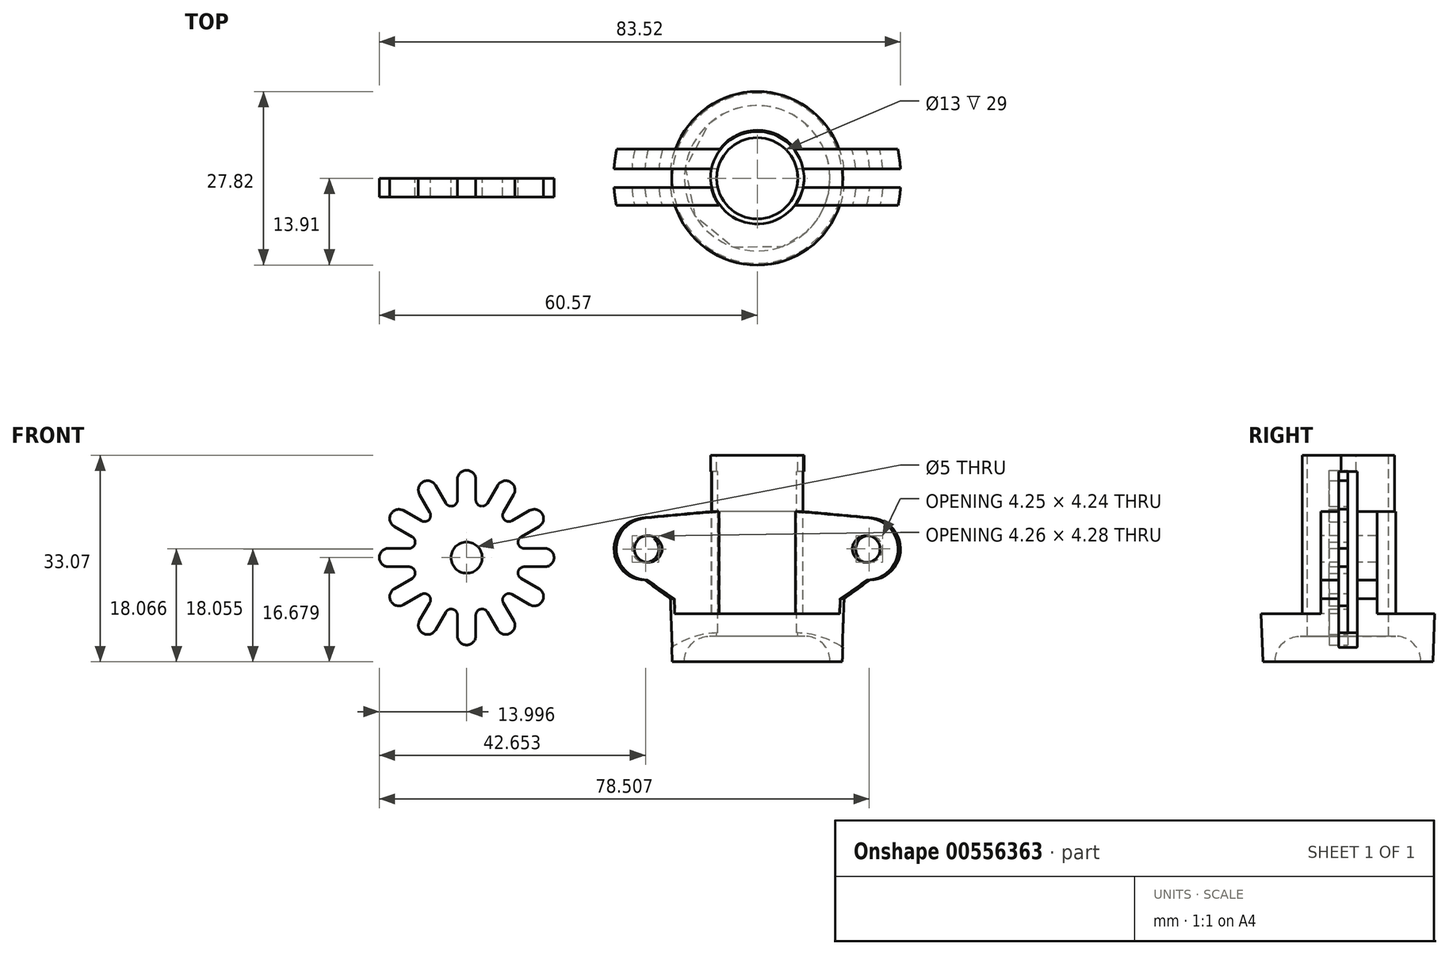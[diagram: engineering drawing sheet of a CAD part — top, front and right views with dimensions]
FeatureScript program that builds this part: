
annotation { "Feature Type Name" : "Feature", "Feature Type Description" : "" }
export const myFeature = defineFeature(function(context is Context, id is Id, definition is map)
    precondition{}
    {
        {
            var Q0;
            Q0=qCreatedBy(makeId("Front.planeOp"),FACE);
            var sketch = newSketch(context, id + "F0", { "sketchPlane" : qUnion([Q0])});
            skLineSegment(sketch, "E0", {"start": v(0, 47.2) * mm, "end": v(7.5, 47.2) * mm, "construction": true});
            skLineSegment(sketch, "E1", {"start": v(0, 38.2) * mm, "end": v(7.5, 38.2) * mm, "construction": true});
            skLineSegment(sketch, "E2", {"start": v(0, 32.2) * mm, "end": v(23, 32.2) * mm, "construction": true});
            skLineSegment(sketch, "E3", {"start": v(0, 24.2) * mm, "end": v(14, 24.2) * mm, "construction": true});
            skLineSegment(sketch, "E4", {"start": v(7.5, 47.2) * mm, "end": v(7.5, 38.2) * mm, "construction": true});
            skCircle(sketch, "E5", {"center": v(18, 32.2) * mm, "radius": 5 * mm, "construction": true});
            skLineSegment(sketch, "E6", {"start": v(7.5, 47.2) * mm, "end": v(7.5, 38.2) * mm});
            skLineSegment(sketch, "E7", {"start": v(7.5, 38.2) * mm, "end": v(18.46, 37.17) * mm});
            skArc(sketch, "E8", {"start": v(18.46, 37.17) * mm, "mid": v(23, 32) * mm, "end": v(18.07, 27.2) * mm});
            skLineSegment(sketch, "E9", {"start": v(18.07, 27.2) * mm, "end": v(14, 24.2) * mm});
            skLineSegment(sketch, "E10", {"start": v(7.5, 47.2) * mm, "end": v(6.5, 47.2) * mm});
            skLineSegment(sketch, "E11", {"start": v(6.5, 47.2) * mm, "end": v(6.5, 18.2) * mm});
            skLineSegment(sketch, "E12", {"start": v(7.66, 18.2) * mm, "end": v(6.5, 18.2) * mm});
            skPoint(sketch, "E13.visualSharp", {"position": v(11.67, 18.2) * mm});
            skArc(sketch, "E13.filletArc", {"start": v(11.66, 14.13) * mm, "mid": v(10.52, 17) * mm, "end": v(7.66, 18.2) * mm});
            skPoint(sketch, "E14", {"position": v(13.63, 14.13) * mm});
            skLineSegment(sketch, "E15", {"start": v(11.66, 14.13) * mm, "end": v(13.63, 14.13) * mm});
            skLineSegment(sketch, "E16", {"start": v(14, 24.2) * mm, "end": v(13.63, 14.13) * mm});
            skLineSegment(sketch, "E17", {"start": v(0, 61.24) * mm, "end": v(0, 0) * mm, "construction": true});
            skCircle(sketch, "E18", {"center": v(18, 32.2) * mm, "radius": 2.15 * mm});
            skSolve(sketch);
        }
        {
            var Q0;
            Q0 = qSketchRegion(id + "F0", true);
            var Q1;
            Q1=sQuery(id+"F0.wireOp",EDGE,"E17");
            revolve(context, id + "F1", {"entities" : qUnion([Q0]), "axis" : qUnion([Q1]), "revolveType" : RevolveType.FULL});
        }
        {
            var Q0;
            Q0=makeQuery(id+"F1.opRevolve","SWEPT_FACE",FACE,{"disambiguationData":[OSD([sQuery(id+"F0.wireOp",EDGE,"E10")])]});
            var sketch = newSketch(context, id + "F2", { "sketchPlane" : qUnion([Q0])});
            skCircle(sketch, "E19.0", {"center": v(0.03, 0.18) * mm, "radius": 7.5 * mm});
            skCircle(sketch, "E20", {"center": v(0.03, 0.18) * mm, "radius": 23.76 * mm});
            skLineSegment(sketch, "E21", {"start": v(25.7, 0.18) * mm, "end": v(-26.86, 0.18) * mm, "construction": true});
            skLineSegment(sketch, "E22", {"start": v(23.36, 4.68) * mm, "end": v(6.03, 4.68) * mm});
            skLineSegment(sketch, "E23.trimOffspring", {"start": v(-5.97, 4.68) * mm, "end": v(-23.3, 4.68) * mm});
            skLineSegment(sketch, "E24.MirrorCS", {"start": v(-5.97, -4.32) * mm, "end": v(-23.3, -4.32) * mm});
            skLineSegment(sketch, "E25.MirrorCS", {"start": v(23.36, -4.32) * mm, "end": v(6.03, -4.32) * mm});
            skSolve(sketch);
        }
        {
            var Q0;
            {var subQ0=sQuery(id+"F2.wireOp",EDGE,"E22");Q0=makeQuery(id+"F2.imprint","IMPRINT",FACE,{"disambiguationData":[TD([[makeQuery(id+"F2.imprint","IMPRINT",EDGE,{"derivedFrom":subQ0}),-1.0]])]});}
            var Q1;
            {var subQ0=sQuery(id+"F2.wireOp",EDGE,"E24.MirrorCS");var subQ1=sQuery(id+"F2.wireOp",EDGE,"E19.0");var subQ2=makeQuery(id+"F2.imprint","INTERSECT",VERTEX,{"derivedFrom":[subQ1,subQ0]});Q1=makeQuery(id+"F2.imprint","IMPRINT",FACE,{"disambiguationData":[TD([[makeQuery(id+"F2.imprint","IMPRINT",EDGE,{"disambiguationData":[TD([[subQ2,1.0]])],"derivedFrom":subQ1}),-1.0]])]});}
            var Q2;
            {var subQ0=sQuery(id+"F2.wireOp",EDGE,"E25.MirrorCS");var subQ1=sQuery(id+"F2.wireOp",EDGE,"E19.0");var subQ2=makeQuery(id+"F2.imprint","INTERSECT",VERTEX,{"derivedFrom":[subQ1,subQ0]});Q2=makeQuery(id+"F2.imprint","IMPRINT",FACE,{"disambiguationData":[TD([[makeQuery(id+"F2.imprint","IMPRINT",EDGE,{"disambiguationData":[TD([[subQ2,-1.0]])],"derivedFrom":subQ1}),-1.0]])]});}
            var Q3;
            {var subQ0=sQuery(id+"F2.wireOp",EDGE,"E24.MirrorCS");var subQ1=sQuery(id+"F2.wireOp",EDGE,"E19.0");var subQ2=makeQuery(id+"F2.imprint","INTERSECT",VERTEX,{"derivedFrom":[subQ1,subQ0]});Q3=makeQuery(id+"F2.imprint","IMPRINT",FACE,{"disambiguationData":[TD([[makeQuery(id+"F2.imprint","IMPRINT",EDGE,{"disambiguationData":[TD([[subQ2,-1.0]])],"derivedFrom":subQ1}),-1.0]])]});}
            var Q4;
            {var subQ0=sQuery(id+"F2.wireOp",EDGE,"E24.MirrorCS");var subQ1=sQuery(id+"F2.wireOp",EDGE,"E20");var subQ2=makeQuery(id+"F2.imprint","INTERSECT",VERTEX,{"derivedFrom":[subQ1,subQ0]});Q4=makeQuery(id+"F2.imprint","IMPRINT",FACE,{"disambiguationData":[TD([[makeQuery(id+"F2.imprint","IMPRINT",EDGE,{"disambiguationData":[TD([[subQ2,-1.0]])],"derivedFrom":subQ1}),1.0]])]});}
            extrude(context, id + "F3", {"entities" : qUnion([Q0, Q1, Q2, Q3, Q4]), "operationType" : NewBodyOperationType.REMOVE, "oppositeDirection" : true, "depth" : 25.4 * mm, "offsetDistance" : 25.4 * mm});
        }
        {
            var Q0;
            Q0=qCreatedBy(makeId("Front.planeOp"),FACE);
            var sketch = newSketch(context, id + "F4", { "sketchPlane" : qUnion([Q0])});
            skArc(sketch, "E26", {"start": v(18.63, 27.23) * mm, "mid": v(23.2, 32.3) * mm, "end": v(18.45, 37.2) * mm});
            skLineSegment(sketch, "E27", {"start": v(9.31, 38.08) * mm, "end": v(18.45, 37.2) * mm});
            skArc(sketch, "E28", {"start": v(7.5, 40.07) * mm, "mid": v(8.02, 38.72) * mm, "end": v(9.31, 38.08) * mm});
            skLineSegment(sketch, "E29", {"start": v(18.63, 27.23) * mm, "end": v(14.84, 24.76) * mm});
            skArc(sketch, "E30", {"start": v(14.84, 24.76) * mm, "mid": v(14.24, 24.07) * mm, "end": v(14, 23.19) * mm});
            skLineSegment(sketch, "E31", {"start": v(0, 54.8) * mm, "end": v(0, 5.85) * mm, "construction": true});
            skLineSegment(sketch, "E32", {"start": v(7.5, 40.07) * mm, "end": v(7.5, 44.62) * mm});
            skLineSegment(sketch, "E33.MirrorCS", {"start": v(-7.5, 40.07) * mm, "end": v(-7.5, 44.62) * mm});
            skArc(sketch, "E34.MirrorCS", {"start": v(-14.84, 24.76) * mm, "mid": v(-14.24, 24.07) * mm, "end": v(-14, 23.19) * mm});
            skLineSegment(sketch, "E35.MirrorCS", {"start": v(-18.63, 27.23) * mm, "end": v(-14.84, 24.76) * mm});
            skArc(sketch, "E36.MirrorCS", {"start": v(-7.5, 40.07) * mm, "mid": v(-8.02, 38.72) * mm, "end": v(-9.31, 38.08) * mm});
            skLineSegment(sketch, "E37.MirrorCS", {"start": v(-9.31, 38.08) * mm, "end": v(-18.45, 37.2) * mm});
            skArc(sketch, "E38.MirrorCS", {"start": v(-18.63, 27.23) * mm, "mid": v(-23.2, 32.3) * mm, "end": v(-18.45, 37.2) * mm});
            skLineSegment(sketch, "E39", {"start": v(7.5, 44.62) * mm, "end": v(-7.5, 44.62) * mm});
            skLineSegment(sketch, "E40", {"start": v(14, 23.19) * mm, "end": v(14, 16.19) * mm});
            skLineSegment(sketch, "E41.0", {"start": v(6, 18.25) * mm, "end": v(6, 40.07) * mm});
            skLineSegment(sketch, "E42.0", {"start": v(-6, 18.25) * mm, "end": v(-6, 40.07) * mm});
            skLineSegment(sketch, "E43.0", {"start": v(6, 18.25) * mm, "end": v(-6, 18.25) * mm});
            skLineSegment(sketch, "E44", {"start": v(6, 18.75) * mm, "end": v(-6, 18.75) * mm});
            skArc(sketch, "E45", {"start": v(14, 16.19) * mm, "mid": v(10.2, 18.1) * mm, "end": v(6, 18.75) * mm});
            skLineSegment(sketch, "E46.MirrorCS", {"start": v(-6, 18.25) * mm, "end": v(6, 18.25) * mm});
            skLineSegment(sketch, "E47.MirrorCS", {"start": v(-14, 23.19) * mm, "end": v(-14, 16.19) * mm});
            skArc(sketch, "E48.MirrorCS", {"start": v(-14, 16.19) * mm, "mid": v(-10.2, 18.1) * mm, "end": v(-6, 18.75) * mm});
            skLineSegment(sketch, "E49.MirrorCS", {"start": v(-7.5, 44.62) * mm, "end": v(7.5, 44.62) * mm});
            skLineSegment(sketch, "E50.MirrorCS", {"start": v(-6, 18.75) * mm, "end": v(6, 18.75) * mm});
            skSolve(sketch);
        }
        {
            var Q0;
            Q0 = qSketchRegion(id + "F4", true);
            extrude(context, id + "F5", {"entities" : qUnion([Q0]), "operationType" : NewBodyOperationType.REMOVE, "endBound" : BoundingType.SYMMETRIC, "depth" : 3 * mm, "offsetDistance" : 25.4 * mm});
        }
        {
            var Q0;
            Q0=qCreatedBy(makeId("Front.planeOp"),FACE);
            var sketch = newSketch(context, id + "F6", { "sketchPlane" : qUnion([Q0])});
            skCircle(sketch, "E51", {"center": v(-46.57, 30.8) * mm, "radius": 2.5 * mm});
            skArc(sketch, "E52", {"start": v(-39.76, 18.58) * mm, "mid": v(-39.48, 42.88) * mm, "end": v(-60.57, 30.8) * mm, "construction": true});
            skLineSegment(sketch, "E53.bottom", {"start": v(-49.07, 30.8) * mm, "end": v(-44.07, 30.8) * mm, "construction": true});
            skLineSegment(sketch, "E53.left", {"start": v(-49.07, 30.8) * mm, "end": v(-49.07, 30.51) * mm, "construction": true});
            skLineSegment(sketch, "E54", {"start": v(-32.57, 30.8) * mm, "end": v(-34.05, 30.8) * mm, "construction": true});
            skLineSegment(sketch, "E55", {"start": v(-55.8, 32.28) * mm, "end": v(-59.1, 32.28) * mm});
            skArc(sketch, "E56", {"start": v(-59.1, 32.28) * mm, "mid": v(-60.57, 30.8) * mm, "end": v(-59.1, 29.33) * mm});
            skLineSegment(sketch, "E57", {"start": v(-59.1, 29.33) * mm, "end": v(-55.8, 29.33) * mm});
            skArc(sketch, "E58.1.0", {"start": v(-56.68, 38.35) * mm, "mid": v(-58.7, 37.81) * mm, "end": v(-58.16, 35.8) * mm});
            skLineSegment(sketch, "E58.1.1", {"start": v(-53.83, 36.7) * mm, "end": v(-56.68, 38.35) * mm});
            skLineSegment(sketch, "E58.1.2", {"start": v(-58.16, 35.8) * mm, "end": v(-55.3, 34.15) * mm});
            skArc(sketch, "E58.2.0", {"start": v(-51.56, 42.4) * mm, "mid": v(-53.57, 42.94) * mm, "end": v(-54.11, 40.92) * mm});
            skLineSegment(sketch, "E58.2.1", {"start": v(-49.91, 39.55) * mm, "end": v(-51.56, 42.4) * mm});
            skLineSegment(sketch, "E58.2.2", {"start": v(-54.11, 40.92) * mm, "end": v(-52.47, 38.07) * mm});
            skArc(sketch, "E58.3.0", {"start": v(-45.1, 43.34) * mm, "mid": v(-46.57, 44.81) * mm, "end": v(-48.05, 43.34) * mm});
            skLineSegment(sketch, "E58.3.1", {"start": v(-45.1, 40.05) * mm, "end": v(-45.1, 43.34) * mm});
            skLineSegment(sketch, "E58.3.2", {"start": v(-48.05, 43.34) * mm, "end": v(-48.05, 40.05) * mm});
            skArc(sketch, "E58.4.0", {"start": v(-39.03, 40.92) * mm, "mid": v(-39.57, 42.94) * mm, "end": v(-41.59, 42.4) * mm});
            skLineSegment(sketch, "E58.4.1", {"start": v(-40.68, 38.07) * mm, "end": v(-39.03, 40.92) * mm});
            skLineSegment(sketch, "E58.4.2", {"start": v(-41.59, 42.4) * mm, "end": v(-43.23, 39.55) * mm});
            skArc(sketch, "E58.5.0", {"start": v(-34.99, 35.8) * mm, "mid": v(-34.45, 37.81) * mm, "end": v(-36.46, 38.35) * mm});
            skLineSegment(sketch, "E58.5.1", {"start": v(-37.84, 34.15) * mm, "end": v(-34.99, 35.8) * mm});
            skLineSegment(sketch, "E58.5.2", {"start": v(-36.46, 38.35) * mm, "end": v(-39.31, 36.7) * mm});
            skArc(sketch, "E58.6.0", {"start": v(-34.05, 29.33) * mm, "mid": v(-32.57, 30.8) * mm, "end": v(-34.05, 32.28) * mm});
            skLineSegment(sketch, "E58.6.1", {"start": v(-37.34, 29.33) * mm, "end": v(-34.05, 29.33) * mm});
            skLineSegment(sketch, "E58.6.2", {"start": v(-34.05, 32.28) * mm, "end": v(-37.34, 32.28) * mm});
            skLineSegment(sketch, "E58.anchor1", {"start": v(-46.57, 30.8) * mm, "end": v(-49.07, 30.51) * mm, "construction": true});
            skLineSegment(sketch, "E58.anchor2", {"start": v(-46.57, 30.8) * mm, "end": v(-44.1, 31.1) * mm, "construction": true});
            skArc(sketch, "E59", {"start": v(-55.8, 32.28) * mm, "mid": v(-54.84, 33.03) * mm, "end": v(-55.3, 34.15) * mm});
            skArc(sketch, "E60.1.0", {"start": v(-53.83, 36.7) * mm, "mid": v(-52.63, 36.86) * mm, "end": v(-52.47, 38.07) * mm});
            skArc(sketch, "E60.2.0", {"start": v(-49.91, 39.55) * mm, "mid": v(-48.79, 39.08) * mm, "end": v(-48.05, 40.05) * mm});
            skArc(sketch, "E60.3.0", {"start": v(-45.1, 40.05) * mm, "mid": v(-44.36, 39.08) * mm, "end": v(-43.23, 39.55) * mm});
            skArc(sketch, "E60.4.0", {"start": v(-40.68, 38.07) * mm, "mid": v(-40.52, 36.86) * mm, "end": v(-39.31, 36.7) * mm});
            skArc(sketch, "E60.5.0", {"start": v(-37.84, 34.15) * mm, "mid": v(-38.3, 33.03) * mm, "end": v(-37.34, 32.28) * mm});
            skLineSegment(sketch, "E60.anchor1", {"start": v(-46.57, 30.8) * mm, "end": v(-49.04, 31.2) * mm, "construction": true});
            skLineSegment(sketch, "E60.anchor2", {"start": v(-46.57, 30.8) * mm, "end": v(-44.1, 30.42) * mm, "construction": true});
            skLineSegment(sketch, "E61.trimOffspring", {"start": v(-41.07, 29.93) * mm, "end": v(-37.34, 29.33) * mm, "construction": true});
            skLineSegment(sketch, "E62.trimOffspring", {"start": v(-44.07, 30.8) * mm, "end": v(-49.07, 30.8) * mm, "construction": true});
            skLineSegment(sketch, "E63", {"start": v(-60.57, 30.8) * mm, "end": v(-32.57, 30.8) * mm, "construction": true});
            skArc(sketch, "E64.MirrorCS", {"start": v(-59.1, 29.33) * mm, "mid": v(-60.57, 30.8) * mm, "end": v(-59.1, 32.28) * mm});
            skLineSegment(sketch, "E65.MirrorCS", {"start": v(-55.8, 29.33) * mm, "end": v(-59.1, 29.33) * mm});
            skArc(sketch, "E66.MirrorCS", {"start": v(-55.8, 29.33) * mm, "mid": v(-54.84, 28.6) * mm, "end": v(-55.3, 27.47) * mm});
            skLineSegment(sketch, "E67.MirrorCS", {"start": v(-58.16, 25.82) * mm, "end": v(-55.3, 27.47) * mm});
            skArc(sketch, "E68.MirrorCS", {"start": v(-56.68, 23.27) * mm, "mid": v(-58.7, 23.8) * mm, "end": v(-58.16, 25.82) * mm});
            skLineSegment(sketch, "E69.MirrorCS", {"start": v(-53.83, 24.91) * mm, "end": v(-56.68, 23.27) * mm});
            skArc(sketch, "E70.MirrorCS", {"start": v(-53.83, 24.91) * mm, "mid": v(-52.63, 24.75) * mm, "end": v(-52.47, 23.55) * mm});
            skLineSegment(sketch, "E71.MirrorCS", {"start": v(-54.11, 20.7) * mm, "end": v(-52.47, 23.55) * mm});
            skArc(sketch, "E72.MirrorCS", {"start": v(-51.56, 19.22) * mm, "mid": v(-53.57, 18.68) * mm, "end": v(-54.11, 20.7) * mm});
            skLineSegment(sketch, "E73.MirrorCS", {"start": v(-49.91, 22.07) * mm, "end": v(-51.56, 19.22) * mm});
            skArc(sketch, "E74.MirrorCS", {"start": v(-49.91, 22.07) * mm, "mid": v(-48.79, 22.54) * mm, "end": v(-48.05, 21.57) * mm});
            skLineSegment(sketch, "E75.MirrorCS", {"start": v(-48.05, 18.28) * mm, "end": v(-48.05, 21.57) * mm});
            skArc(sketch, "E76.MirrorCS", {"start": v(-45.1, 18.28) * mm, "mid": v(-46.57, 16.8) * mm, "end": v(-48.05, 18.28) * mm});
            skLineSegment(sketch, "E77.MirrorCS", {"start": v(-45.1, 21.57) * mm, "end": v(-45.1, 18.28) * mm});
            skArc(sketch, "E78.MirrorCS", {"start": v(-45.1, 21.57) * mm, "mid": v(-44.36, 22.54) * mm, "end": v(-43.23, 22.07) * mm});
            skLineSegment(sketch, "E79.MirrorCS", {"start": v(-41.59, 19.22) * mm, "end": v(-43.23, 22.07) * mm});
            skArc(sketch, "E80.MirrorCS", {"start": v(-39.03, 20.7) * mm, "mid": v(-39.57, 18.68) * mm, "end": v(-41.59, 19.22) * mm});
            skLineSegment(sketch, "E81.MirrorCS", {"start": v(-40.68, 23.55) * mm, "end": v(-39.03, 20.7) * mm});
            skArc(sketch, "E82.MirrorCS", {"start": v(-40.68, 23.55) * mm, "mid": v(-40.52, 24.75) * mm, "end": v(-39.31, 24.91) * mm});
            skLineSegment(sketch, "E83.MirrorCS", {"start": v(-36.46, 23.27) * mm, "end": v(-39.31, 24.91) * mm});
            skArc(sketch, "E84.MirrorCS", {"start": v(-34.99, 25.82) * mm, "mid": v(-34.45, 23.8) * mm, "end": v(-36.46, 23.27) * mm});
            skLineSegment(sketch, "E85.MirrorCS", {"start": v(-37.84, 27.47) * mm, "end": v(-34.99, 25.82) * mm});
            skArc(sketch, "E86.MirrorCS", {"start": v(-37.84, 27.47) * mm, "mid": v(-38.3, 28.6) * mm, "end": v(-37.34, 29.33) * mm});
            skSolve(sketch);
        }
        {
            var Q0;
            Q0=makeQuery(id+"F6.imprint","IMPRINT",FACE,{"disambiguationData":[TD([[makeQuery(id+"F6.imprint","IMPRINT",EDGE,{"derivedFrom":sQuery(id+"F6.wireOp",EDGE,"E51")}),-1.0]])]});
            extrude(context, id + "F7", {"entities" : qUnion([Q0]), "depth" : 3 * mm, "offsetDistance" : 25.4 * mm});
        }
    });
